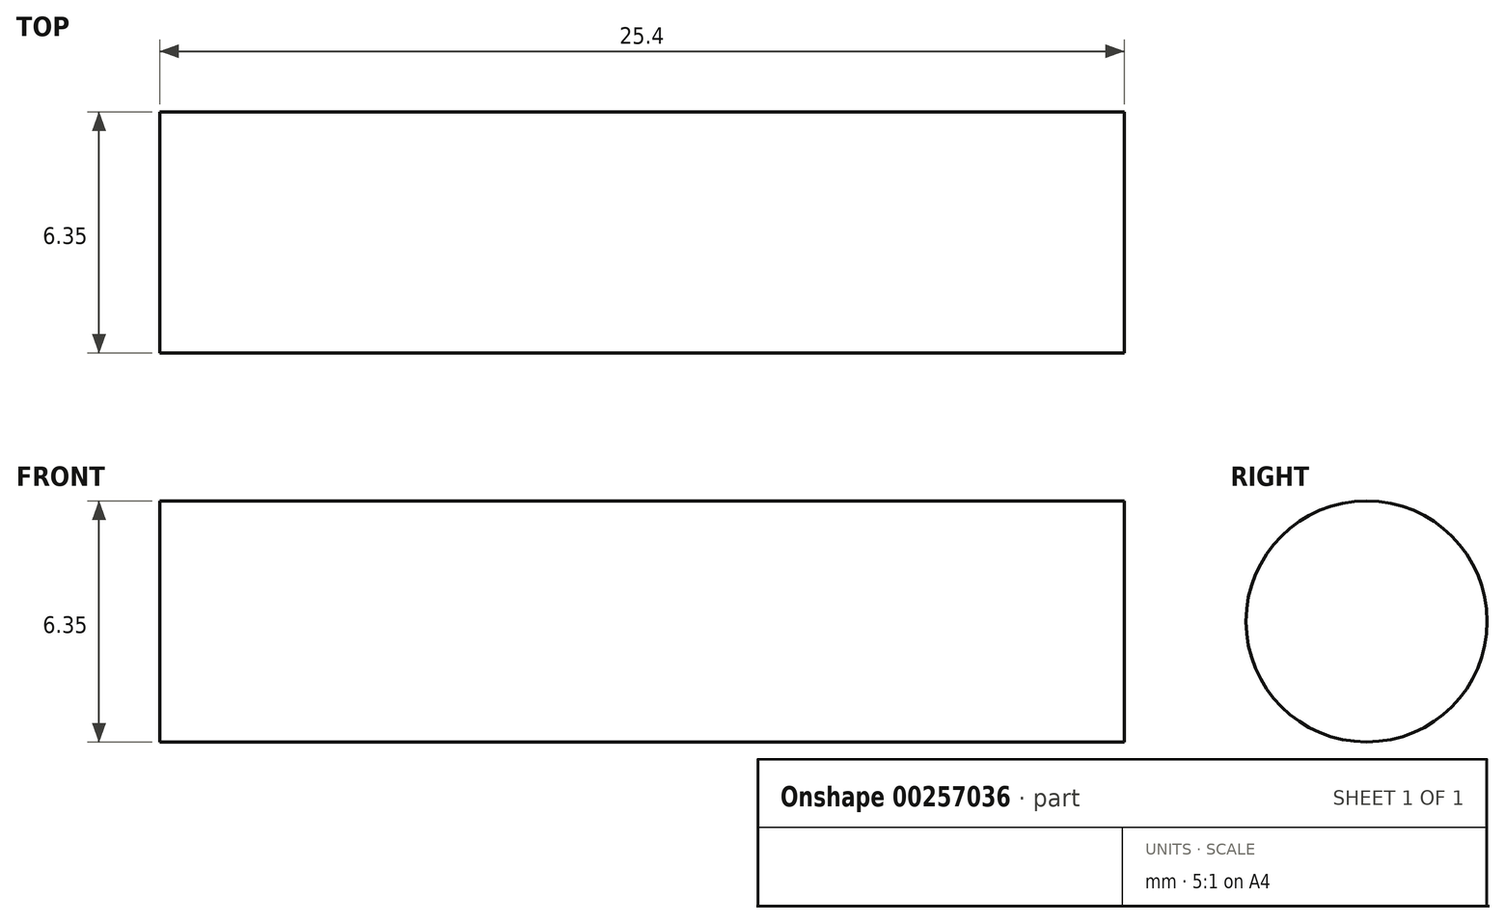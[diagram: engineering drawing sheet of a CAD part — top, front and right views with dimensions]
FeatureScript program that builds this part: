
annotation { "Feature Type Name" : "Feature", "Feature Type Description" : "" }
export const myFeature = defineFeature(function(context is Context, id is Id, definition is map)
    precondition{}
    {
        {
            var Q0;
            Q0=qCreatedBy(makeId("Right.planeOp"),FACE);
            var sketch = newSketch(context, id + "F0", { "sketchPlane" : qUnion([Q0])});
            skCircle(sketch, "E0", {"center": v(-37.76, 26.19) * mm, "radius": 3.18 * mm});
            skSolve(sketch);
        }
        {
            var Q0;
            Q0 = qSketchRegion(id + "F0", true);
            extrude(context, id + "F1", {"entities" : qUnion([Q0]), "depth" : 25.4 * mm});
        }
    });
